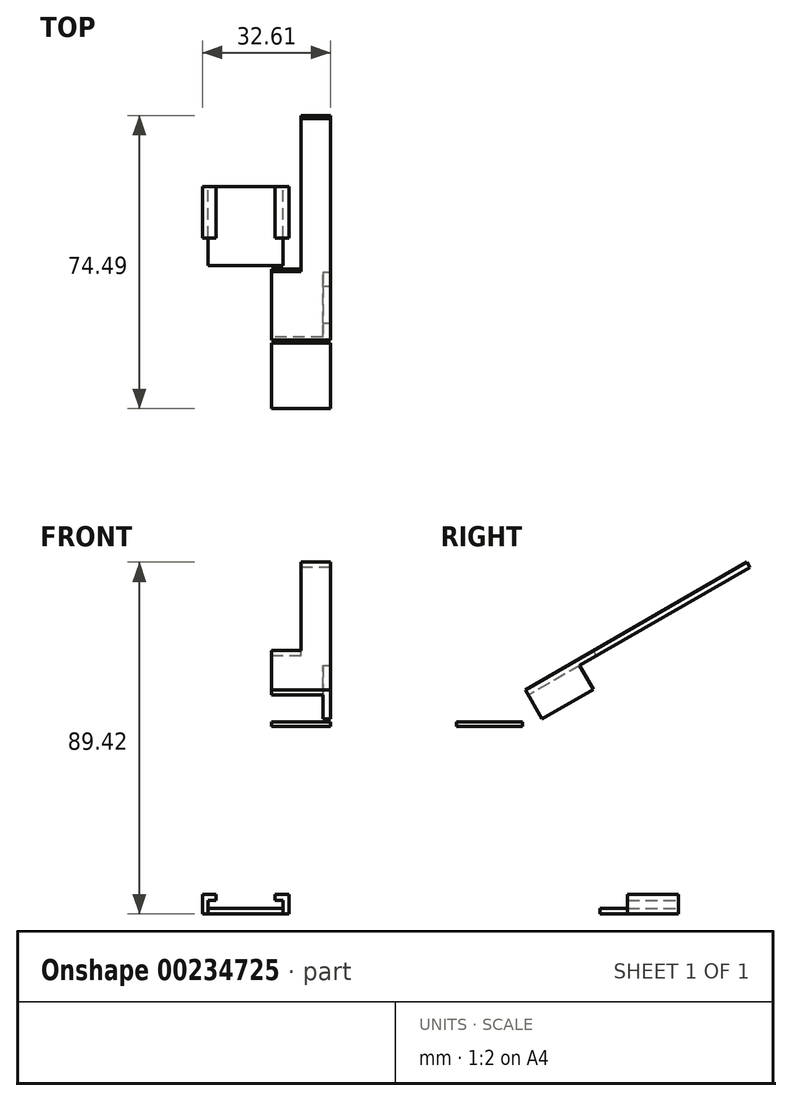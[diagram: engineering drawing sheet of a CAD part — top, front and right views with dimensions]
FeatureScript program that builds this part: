
annotation { "Feature Type Name" : "Feature", "Feature Type Description" : "" }
export const myFeature = defineFeature(function(context is Context, id is Id, definition is map)
    precondition{}
    {
        {
            var Q0;
            Q0=qCreatedBy(makeId("Front.planeOp"),FACE);
            var sketch = newSketch(context, id + "F0", { "sketchPlane" : qUnion([Q0])});
            skLineSegment(sketch, "E0", {"start": v(-16.11, -29.67) * mm, "end": v(2.89, -29.67) * mm});
            skLineSegment(sketch, "E1", {"start": v(2.89, -29.67) * mm, "end": v(2.89, -27.67) * mm});
            skLineSegment(sketch, "E2", {"start": v(2.89, -27.67) * mm, "end": v(0.89, -27.67) * mm});
            skLineSegment(sketch, "E3", {"start": v(0.89, -27.67) * mm, "end": v(0.89, -26.17) * mm});
            skLineSegment(sketch, "E4", {"start": v(0.89, -26.17) * mm, "end": v(4.39, -26.17) * mm});
            skLineSegment(sketch, "E5", {"start": v(4.39, -26.17) * mm, "end": v(4.39, -31.17) * mm});
            skLineSegment(sketch, "E6", {"start": v(4.39, -31.17) * mm, "end": v(-17.61, -31.17) * mm});
            skLineSegment(sketch, "E7", {"start": v(-17.61, -31.17) * mm, "end": v(-17.61, -26.17) * mm});
            skLineSegment(sketch, "E8", {"start": v(-17.61, -26.17) * mm, "end": v(-14.11, -26.17) * mm});
            skLineSegment(sketch, "E9", {"start": v(-14.11, -26.17) * mm, "end": v(-14.11, -27.67) * mm});
            skLineSegment(sketch, "E10", {"start": v(-14.11, -27.67) * mm, "end": v(-16.11, -27.67) * mm});
            skLineSegment(sketch, "E11", {"start": v(-16.11, -27.67) * mm, "end": v(-16.11, -29.67) * mm});
            skLineSegment(sketch, "E12", {"start": v(2.89, -29.67) * mm, "end": v(2.89, -31.17) * mm});
            skLineSegment(sketch, "E13", {"start": v(-16.11, -29.67) * mm, "end": v(-16.11, -31.17) * mm});
            skSolve(sketch);
        }
        {
            var Q0;
            {var subQ0=sQuery(id+"F0.wireOp",EDGE,"E7");Q0=makeQuery(id+"F0.imprint","IMPRINT",FACE,{"disambiguationData":[TD([[makeQuery(id+"F0.imprint","IMPRINT",EDGE,{"derivedFrom":subQ0}),-1.0]])]});}
            var Q1;
            Q1=makeQuery(id+"F0.imprint","IMPRINT",FACE,{"disambiguationData":[TD([[makeQuery(id+"F0.imprint","IMPRINT",EDGE,{"derivedFrom":sQuery(id+"F0.wireOp",EDGE,"E1")}),-1.0]])]});
            extrude(context, id + "F1", {"entities" : qUnion([Q0, Q1]), "depth" : 13 * mm});
        }
        {
            var Q0;
            Q0=makeQuery(id+"F0.imprint","IMPRINT",FACE,{"disambiguationData":[TD([[makeQuery(id+"F0.imprint","IMPRINT",EDGE,{"derivedFrom":sQuery(id+"F0.wireOp",EDGE,"E0")}),-1.0]])]});
            extrude(context, id + "F2", {"entities" : qUnion([Q0]), "operationType" : NewBodyOperationType.ADD, "depth" : 20 * mm});
        }
        {
            var Q0;
            Q0=qCreatedBy(makeId("Right.planeOp"),FACE);
            var sketch = newSketch(context, id + "F3", { "sketchPlane" : qUnion([Q0])});
            skLineSegment(sketch, "E14", {"start": v(-68.93, -63.56) * mm, "end": v(-68.93, -47.15) * mm});
            skLineSegment(sketch, "E15", {"start": v(-68.93, -47.15) * mm, "end": v(-38.93, -47.15) * mm});
            skLineSegment(sketch, "E16", {"start": v(-38.93, -47.15) * mm, "end": v(-21.6, -37.15) * mm});
            skLineSegment(sketch, "E17", {"start": v(-21.6, -37.15) * mm, "end": v(-20.86, -38.45) * mm});
            skLineSegment(sketch, "E18", {"start": v(-20.86, -38.45) * mm, "end": v(-38.93, -48.88) * mm});
            skLineSegment(sketch, "E19", {"start": v(-38.93, -48.88) * mm, "end": v(-67.43, -48.88) * mm});
            skLineSegment(sketch, "E20", {"start": v(-67.43, -48.88) * mm, "end": v(-67.43, -63.56) * mm});
            skLineSegment(sketch, "E21", {"start": v(-67.43, -63.56) * mm, "end": v(-68.93, -63.56) * mm});
            skLineSegment(sketch, "E22", {"start": v(-38.93, -47.15) * mm, "end": v(-38.18, -48.45) * mm});
            skSolve(sketch);
        }
        {
            var Q0;
            Q0=makeQuery(id+"F3.imprint","IMPRINT",FACE,{"disambiguationData":[TD([[makeQuery(id+"F3.imprint","IMPRINT",EDGE,{"derivedFrom":sQuery(id+"F3.wireOp",EDGE,"E16")}),-1.0]])]});
            extrude(context, id + "F4", {"entities" : qUnion([Q0]), "depth" : 15 * mm});
        }
        {
            var Q0;
            Q0=makeQuery(id+"F4.opExtrude","SWEPT_BODY",BODY,{"disambiguationData":[OSD([sQuery(id+"F3.wireOp",EDGE,"E14"),sQuery(id+"F3.wireOp",EDGE,"E15"),sQuery(id+"F3.wireOp",EDGE,"E16"),sQuery(id+"F3.wireOp",EDGE,"E17"),sQuery(id+"F3.wireOp",EDGE,"E18"),sQuery(id+"F3.wireOp",EDGE,"E19"),sQuery(id+"F3.wireOp",EDGE,"E20"),sQuery(id+"F3.wireOp",EDGE,"E21")])]});
            transform(context, id + "F5", {"entities" : qUnion([Q0]), "transformType" : TransformType.TRANSLATION_3D, "dx" : 0 * mm, "dy" : 0 * mm, "dz" : 72.9 * mm, "makeCopy" : false});
        }
        {
            var Q0;
            Q0=makeQuery(id+"F4.opExtrude","SWEPT_FACE",FACE,{"disambiguationData":[OSD([sQuery(id+"F3.wireOp",EDGE,"E17")])]});
            var sketch = newSketch(context, id + "F6", { "sketchPlane" : qUnion([Q0])});
            skLineSegment(sketch, "E23", {"start": v(-15, 41.77) * mm, "end": v(-15, 40.27) * mm});
            skLineSegment(sketch, "E24", {"start": v(-15, 40.27) * mm, "end": v(-7.5, 40.27) * mm});
            skLineSegment(sketch, "E25", {"start": v(-7.5, 40.27) * mm, "end": v(-7.5, 41.77) * mm});
            skLineSegment(sketch, "E26", {"start": v(-7.5, 41.77) * mm, "end": v(-15, 41.77) * mm});
            skSolve(sketch);
        }
        {
            var Q0;
            Q0=makeQuery(id+"F6.imprint","IMPRINT",FACE,{"disambiguationData":[TD([[makeQuery(id+"F6.imprint","IMPRINT",EDGE,{"derivedFrom":sQuery(id+"F6.wireOp",EDGE,"E23")}),1.0]])]});
            extrude(context, id + "F7", {"entities" : qUnion([Q0]), "operationType" : NewBodyOperationType.ADD, "depth" : 45 * mm});
        }
        {
            var Q0;
            Q0=makeQuery(id+"F7.boolean.opBoolean","MERGE",FACE,{"derivedFrom":[makeQuery(id+"F4.opExtrude","CAP_FACE",FACE,{"disambiguationData":[OSD([sQuery(id+"F3.wireOp",EDGE,"E14"),sQuery(id+"F3.wireOp",EDGE,"E15"),sQuery(id+"F3.wireOp",EDGE,"E16"),sQuery(id+"F3.wireOp",EDGE,"E17"),sQuery(id+"F3.wireOp",EDGE,"E18"),sQuery(id+"F3.wireOp",EDGE,"E19"),sQuery(id+"F3.wireOp",EDGE,"E20"),sQuery(id+"F3.wireOp",EDGE,"E21")])],"isStart":false}),makeQuery(id+"F7.opExtrude","SWEPT_FACE",FACE,{"disambiguationData":[OSD([sQuery(id+"F6.wireOp",EDGE,"E23")])]})]});
            var sketch = newSketch(context, id + "F8", { "sketchPlane" : qUnion([Q0])});
            skLineSegment(sketch, "E27", {"start": v(-38.18, 24.45) * mm, "end": v(-38.18, 16.45) * mm});
            skLineSegment(sketch, "E28", {"start": v(-38.18, 16.45) * mm, "end": v(-56.38, 16.45) * mm});
            skLineSegment(sketch, "E29", {"start": v(-56.38, 16.45) * mm, "end": v(-56.38, 24.45) * mm});
            skLineSegment(sketch, "E30.0", {"start": v(-38.93, 17.7) * mm, "end": v(-57.13, 17.7) * mm});
            skLineSegment(sketch, "E31.0", {"start": v(-39.68, 24.45) * mm, "end": v(-39.68, 16.45) * mm});
            skLineSegment(sketch, "E32.0", {"start": v(-54.88, 16.45) * mm, "end": v(-54.88, 24.45) * mm});
            skSolve(sketch);
        }
        {
            var Q0;
            {var subQ0=sQuery(id+"F8.wireOp",EDGE,"E27");var subQ3=sQuery(id+"F8.wireOp",EDGE,"E30.0");var subQ4=makeQuery(id+"F8.imprint","INTERSECT",VERTEX,{"derivedFrom":[subQ0,subQ3]});Q0=makeQuery(id+"F8.imprint","IMPRINT",FACE,{"disambiguationData":[TD([[makeQuery(id+"F8.imprint","IMPRINT",EDGE,{"disambiguationData":[TD([[subQ4,-1.0]])],"derivedFrom":subQ3}),-1.0]])]});}
            var Q1;
            {var subQ0=sQuery(id+"F8.wireOp",EDGE,"E31.0");var subQ1=sQuery(id+"F8.wireOp",EDGE,"E28");var subQ2=makeQuery(id+"F8.imprint","INTERSECT",VERTEX,{"derivedFrom":[subQ1,subQ0]});Q1=makeQuery(id+"F8.imprint","IMPRINT",FACE,{"disambiguationData":[TD([[makeQuery(id+"F8.imprint","IMPRINT",EDGE,{"disambiguationData":[TD([[subQ2,-1.0]])],"derivedFrom":subQ1}),-1.0]])]});}
            var Q2;
            {var subQ0=sQuery(id+"F8.wireOp",EDGE,"E29");var subQ1=makeQuery(id+"F4.opExtrude","CAP_EDGE",EDGE,{"disambiguationData":[OSD([sQuery(id+"F3.wireOp",EDGE,"E19")])],"isStart":false});var subQ2=makeQuery(id+"F8.imprint","INTERSECT",VERTEX,{"derivedFrom":[subQ1,subQ0]});Q2=makeQuery(id+"F8.imprint","IMPRINT",FACE,{"disambiguationData":[TD([[makeQuery(id+"F8.imprint","IMPRINT",EDGE,{"disambiguationData":[TD([[subQ2,1.0]])],"derivedFrom":subQ0}),-1.0]])]});}
            var Q3;
            {var subQ0=sQuery(id+"F8.wireOp",EDGE,"E29");var subQ1=sQuery(id+"F8.wireOp",EDGE,"E28");var subQ2=makeQuery(id+"F8.imprint","INTERSECT",VERTEX,{"derivedFrom":[subQ1,subQ0]});Q3=makeQuery(id+"F8.imprint","IMPRINT",FACE,{"disambiguationData":[TD([[makeQuery(id+"F8.imprint","IMPRINT",EDGE,{"disambiguationData":[TD([[subQ2,1.0]])],"derivedFrom":subQ1}),-1.0]])]});}
            var Q4;
            {var subQ0=sQuery(id+"F8.wireOp",EDGE,"E28");var subQ1=sQuery(id+"F8.wireOp",EDGE,"E27");var subQ2=makeQuery(id+"F8.imprint","INTERSECT",VERTEX,{"derivedFrom":[subQ1,subQ0]});Q4=makeQuery(id+"F8.imprint","IMPRINT",FACE,{"disambiguationData":[TD([[makeQuery(id+"F8.imprint","IMPRINT",EDGE,{"disambiguationData":[TD([[subQ2,1.0]])],"derivedFrom":subQ1}),-1.0]])]});}
            extrude(context, id + "F9", {"entities" : qUnion([Q0, Q1, Q2, Q3, Q4]), "operationType" : NewBodyOperationType.ADD, "oppositeDirection" : true, "depth" : 15 * mm});
        }
        {
            var Q0;
            Q0=makeQuery(id+"F7.boolean.opBoolean","MERGE",FACE,{"derivedFrom":[makeQuery(id+"F4.opExtrude","CAP_FACE",FACE,{"disambiguationData":[OSD([sQuery(id+"F3.wireOp",EDGE,"E16"),sQuery(id+"F3.wireOp",EDGE,"E17"),sQuery(id+"F3.wireOp",EDGE,"E18"),sQuery(id+"F3.wireOp",EDGE,"E22")])],"isStart":false}),makeQuery(id+"F7.opExtrude","SWEPT_FACE",FACE,{"disambiguationData":[OSD([sQuery(id+"F6.wireOp",EDGE,"E23")])]})]});
            var sketch = newSketch(context, id + "F10", { "sketchPlane" : qUnion([Q0])});
            skLineSegment(sketch, "E33", {"start": v(-38.18, 24.45) * mm, "end": v(-34.68, 18.4) * mm});
            skLineSegment(sketch, "E34", {"start": v(-34.68, 18.4) * mm, "end": v(-21.69, 25.9) * mm});
            skLineSegment(sketch, "E35", {"start": v(-21.69, 25.9) * mm, "end": v(-25.19, 31.95) * mm});
            skSolve(sketch);
        }
        {
            var Q0;
            {var subQ0=sQuery(id+"F10.wireOp",EDGE,"E33");Q0=makeQuery(id+"F10.imprint","IMPRINT",FACE,{"disambiguationData":[TD([[makeQuery(id+"F10.imprint","IMPRINT",EDGE,{"derivedFrom":subQ0}),1.0]])]});}
            extrude(context, id + "F11", {"entities" : qUnion([Q0]), "operationType" : NewBodyOperationType.ADD, "oppositeDirection" : true, "depth" : 2 * mm});
        }
    });
